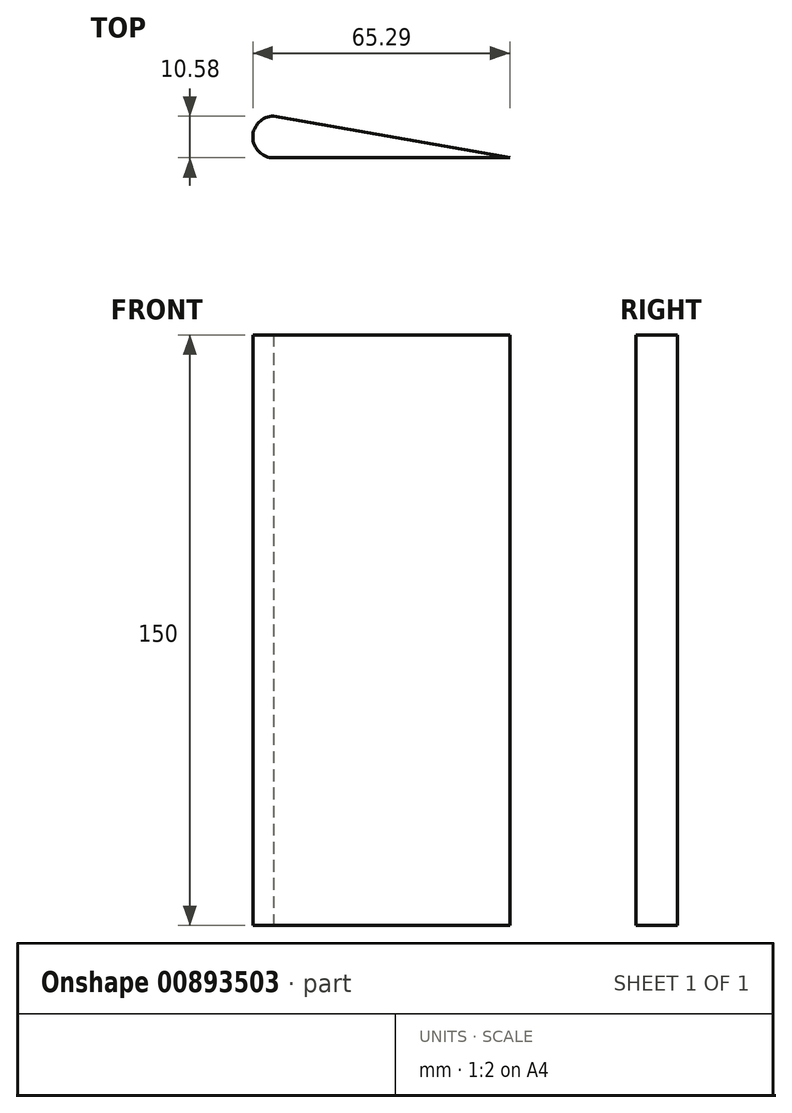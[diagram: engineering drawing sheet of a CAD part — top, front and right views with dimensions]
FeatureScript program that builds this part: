
annotation { "Feature Type Name" : "Feature", "Feature Type Description" : "" }
export const myFeature = defineFeature(function(context is Context, id is Id, definition is map)
    precondition{}
    {
        {
            var Q0;
            Q0=qCreatedBy(makeId("Top.planeOp"),FACE);
            var sketch = newSketch(context, id + "F0", { "sketchPlane" : qUnion([Q0])});
            skLineSegment(sketch, "E0", {"start": v(0, 0) * mm, "end": v(60, 0) * mm});
            skLineSegment(sketch, "E1", {"start": v(60, 0) * mm, "end": v(0, 10.58) * mm});
            skArc(sketch, "E2", {"start": v(0, 0) * mm, "mid": v(-5.29, 5.29) * mm, "end": v(0, 10.58) * mm});
            skSolve(sketch);
        }
        {
            var Q0;
            Q0=makeQuery(id+"F0.imprint","IMPRINT",FACE,{"disambiguationData":[TD([[makeQuery(id+"F0.imprint","IMPRINT",EDGE,{"derivedFrom":sQuery(id+"F0.wireOp",EDGE,"E0")}),1.0]])]});
            extrude(context, id + "F1", {"entities" : qUnion([Q0]), "depth" : 150 * mm, "offsetDistance" : 25.4 * mm});
        }
    });
